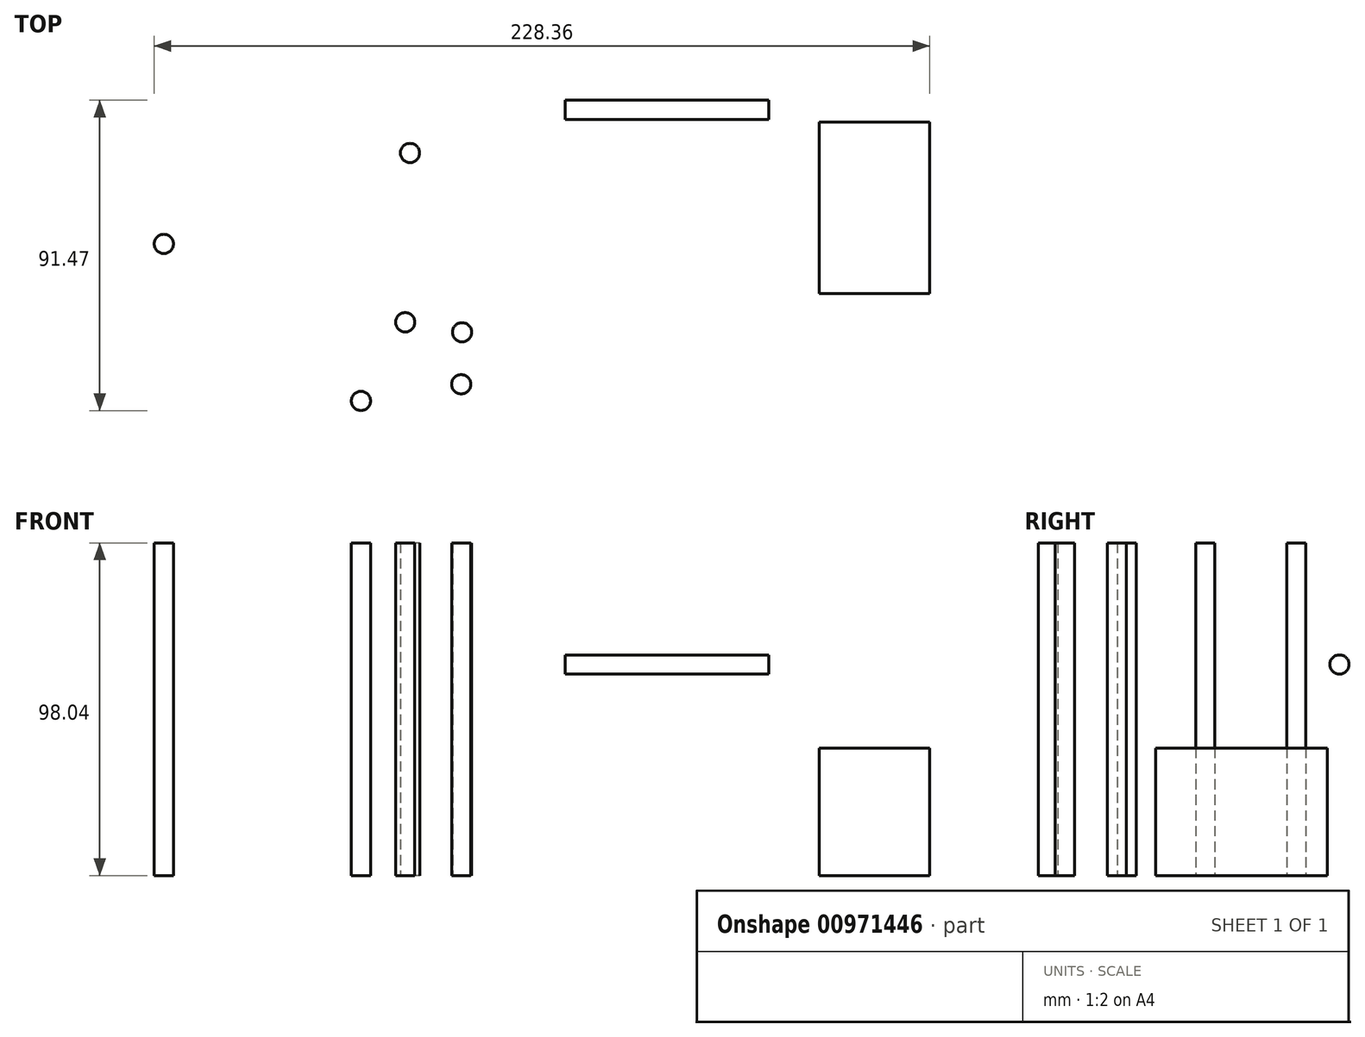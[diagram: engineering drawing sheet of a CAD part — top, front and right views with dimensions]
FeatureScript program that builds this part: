
annotation { "Feature Type Name" : "Feature", "Feature Type Description" : "" }
export const myFeature = defineFeature(function(context is Context, id is Id, definition is map)
    precondition{}
    {
        {
            var Q0;
            Q0=qCreatedBy(makeId("Top.planeOp"),FACE);
            var sketch = newSketch(context, id + "F0", { "sketchPlane" : qUnion([Q0])});
            skCircle(sketch, "E0", {"center": v(-45.63, 22.4) * mm, "radius": 2.84 * mm});
            skCircle(sketch, "E1", {"center": v(-47.04, -27.5) * mm, "radius": 2.84 * mm});
            skCircle(sketch, "E2", {"center": v(-30.3, -30.44) * mm, "radius": 2.84 * mm});
            skCircle(sketch, "E3", {"center": v(-30.55, -45.77) * mm, "radius": 2.84 * mm});
            skCircle(sketch, "E4", {"center": v(-118.12, -4.4) * mm, "radius": 2.84 * mm});
            skCircle(sketch, "E5", {"center": v(-60.08, -50.68) * mm, "radius": 2.84 * mm});
            skSolve(sketch);
        }
        {
            var Q0;
            Q0 = qSketchRegion(id + "F0", true);
            extrude(context, id + "F1", {"entities" : qUnion([Q0]), "depth" : 98.04 * mm, "offsetDistance" : 25.4 * mm});
        }
        {
            var Q0;
            Q0=qCreatedBy(makeId("Top.planeOp"),FACE);
            var sketch = newSketch(context, id + "F2", { "sketchPlane" : qUnion([Q0])});
            skLineSegment(sketch, "E6.bottom", {"start": v(107.4, 31.57) * mm, "end": v(74.83, 31.57) * mm});
            skLineSegment(sketch, "E6.top", {"start": v(107.4, -19.04) * mm, "end": v(74.83, -19.04) * mm});
            skLineSegment(sketch, "E6.left", {"start": v(107.4, 31.57) * mm, "end": v(107.4, -19.04) * mm});
            skLineSegment(sketch, "E6.right", {"start": v(74.83, 31.57) * mm, "end": v(74.83, -19.04) * mm});
            skLineSegment(sketch, "E7.bottom", {"start": v(162.31, 21.9) * mm, "end": v(129.74, 21.9) * mm});
            skLineSegment(sketch, "E7.top", {"start": v(162.31, -28.7) * mm, "end": v(129.74, -28.7) * mm});
            skLineSegment(sketch, "E7.left", {"start": v(162.31, 21.9) * mm, "end": v(162.31, -28.7) * mm});
            skLineSegment(sketch, "E7.right", {"start": v(129.74, 21.9) * mm, "end": v(129.74, -28.7) * mm});
            skSolve(sketch);
        }
        {
            var Q0;
            Q0=makeQuery(id+"F2.imprint","IMPRINT",FACE,{"disambiguationData":[TD([[makeQuery(id+"F2.imprint","IMPRINT",EDGE,{"derivedFrom":sQuery(id+"F2.wireOp",EDGE,"E6.bottom")}),1.0]])]});
            extrude(context, id + "F3", {"entities" : qUnion([Q0]), "depth" : 37.6 * mm, "offsetDistance" : 25.4 * mm});
        }
        {
            var Q0;
            Q0=qCreatedBy(makeId("Right.planeOp"),FACE);
            var sketch = newSketch(context, id + "F4", { "sketchPlane" : qUnion([Q0])});
            skCircle(sketch, "E8", {"center": v(35.11, 62.2) * mm, "radius": 2.84 * mm});
            skSolve(sketch);
        }
        {
            var Q0;
            Q0=makeQuery(id+"F4.imprint","IMPRINT",FACE,{"disambiguationData":[TD([[makeQuery(id+"F4.imprint","IMPRINT",EDGE,{"derivedFrom":sQuery(id+"F4.wireOp",EDGE,"E8")}),1.0]])]});
            extrude(context, id + "F5", {"entities" : qUnion([Q0]), "depth" : 59.94 * mm, "offsetDistance" : 25.4 * mm});
        }
    });
